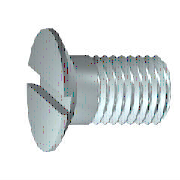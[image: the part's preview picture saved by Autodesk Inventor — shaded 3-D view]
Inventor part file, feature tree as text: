
AUTODESK INVENTOR PART (.ipt)
format: ipt  version: 2017 (Build 210142000, 142)  size: 175,104 bytes
history: native  units: mm (DEFAULTED — no unit token found)
features: sketch x2, extrude x1, plane x1
ambient origin geometry x7: Origin, YZ Plane, XZ Plane, X Axis, Y Axis, Z Axis, Center Point
bodies: Solid1 (feature_tree), Body (feature_tree)
feature tree (4):
  extrude  "Slot"  Depth=5.0mm
  plane  "Work Plane1"
  sketch  "Sketch1"  dims[d0=5.0mm d1=45.0deg d2=0.276053mm d3=2.6mm d4=1.5mm d5=1.947895mm]
  sketch  "Sketch2"  dims[d6=2.5mm d7=4.4mm d19=90.0deg d8=0.5mm d9=0.0mm d10=2.6mm d11=0.0mm d12=0.276052mm d13=0.138026mm d15=0.8mm d16=4.4mm d17=0.0mm d35=45.0deg d39=0.0mm d40=0.0mm]
